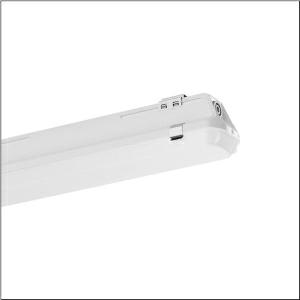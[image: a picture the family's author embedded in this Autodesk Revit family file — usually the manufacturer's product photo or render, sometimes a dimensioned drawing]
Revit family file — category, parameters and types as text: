
# Revit family: monsun_r__11_emergency_51fp207p467h3g_ea6c
name_source: partatom
category: Lighting Fixtures
units: mm (PartAtom-declared; Revit-internal decimal feet)

## family parameters
Cut with Voids When Loaded = No
Host = Face
Light Source = No
Part Type = Normal
Room Calculation Point = No
Round Connector Dimension = Use Diameter
Shared = No

## types (1)
- Monsun® 11 emergency (1 x LED, 5450 lm, 37.2 W, 4000K)
    Apparent Load = 37 VA
    CIE Flux Codes = 45 75 93 94 100
    Color Rendering = 80
    Color Temperature = 4000K
    Default Elevation = 1800 mm
    Description = Monsun® 11 emergency, damp-proof luminaire, chain hanger, primary optical cover: enclosure, of PC, light emission: direct distribution, primary light characteristic: symmetric, installation type: suspended mounting, surface-mounted, horizontal mounting, vertical mounting, LED, rated luminous flux: 5.450lm, luminous efficacy: 147lm/W, light colour: 840, colour temperature: 4000K, control gear: ECG, with terminal, 4-pole, max. 2.5mm², mains connection: 220..240V, AC, 50/60Hz, rated input power: 37W, control gear: single battery element, battery: NiCd, 4,5Ah, mains connection: 230V, luminaire housing, of glass-fibre reinforced polyester, uncoated, bright grey, incl. chain hanger, length: 1.590mm, width: 90mm, height: 88mm, clip for enclosure, of stainless steel (V2A), ceiling mounting element, of stainless steel (V2A), chain hanger, of stainless steel (V2A), protection rating (complete): IP66, insulation class (complete): insulation class I (protective earthing), certification: CE, UKCA, protection symbol: D, impact resistance: IK08, permissible operating ambient temperature: +5..+35°C, standard: EN 50419, EN 60598-2-1, EN 60598-2-22, no direct snow, no direct sun, no direct rain, for indoor or canopied outdoor use, corresponds to IFS (International Featured Standards) requirements for safety and quality in the food industry, contact your sales advisor before using the luminaires in applications with unclear chemical exposure, large temperature fluctuations or condensation-forming humidity, LABS conformity tested according to VDMA 24364:2018-05, packaging unit: 1 piece
    Height = 89 mm
    Lamp = 1 x LED
    Lamp Light Flux = 5450 lm
    Lamp Power = 37.2 W
    Lamp count = 1
    Length = 1590 mm
    Luminous efficacy = 147 lm/W
    Manufacturer = Siteco
    ModVariant = No
    Model = 51FP207P467H3G
    Mounting Place = Ceiling
    Mounting Type = Surface mounted
    Number of Poles = 1
    OnlyDefault = Yes
    Power Factor = 1
    Product Name = Monsun® 11 emergency
    Product group = damp-proof luminaire
    ProductGroupID = 300
    Protection Class = Protection class I
    Protection Degree = IP 66
    RLX_Detail_Level = 1
    RLX_Emergency_Light_Flux = 0 lm
    RLX_Emergency_Type = 0
    RLX_Emergency_Type_DB = No
    RlxData = <blob elided: 89037 chars, md5=859be9d8>
    Socket = socket
    Standby Power = 0 W
    System Light Flux = 5450 lm
    System Power = 37 W
    Type Comments = Product without accessories
    Type Image = l_1004748.jpg
    URL = http://relux.com
    VarID = ---
    Voltage = 0 V
    Weight = 0.00 kg
    Width = 90 mm

## geometry (parser evidence)
native form markers: Blend x4, Sweep x15
no freeform markers — native parametric forms only
